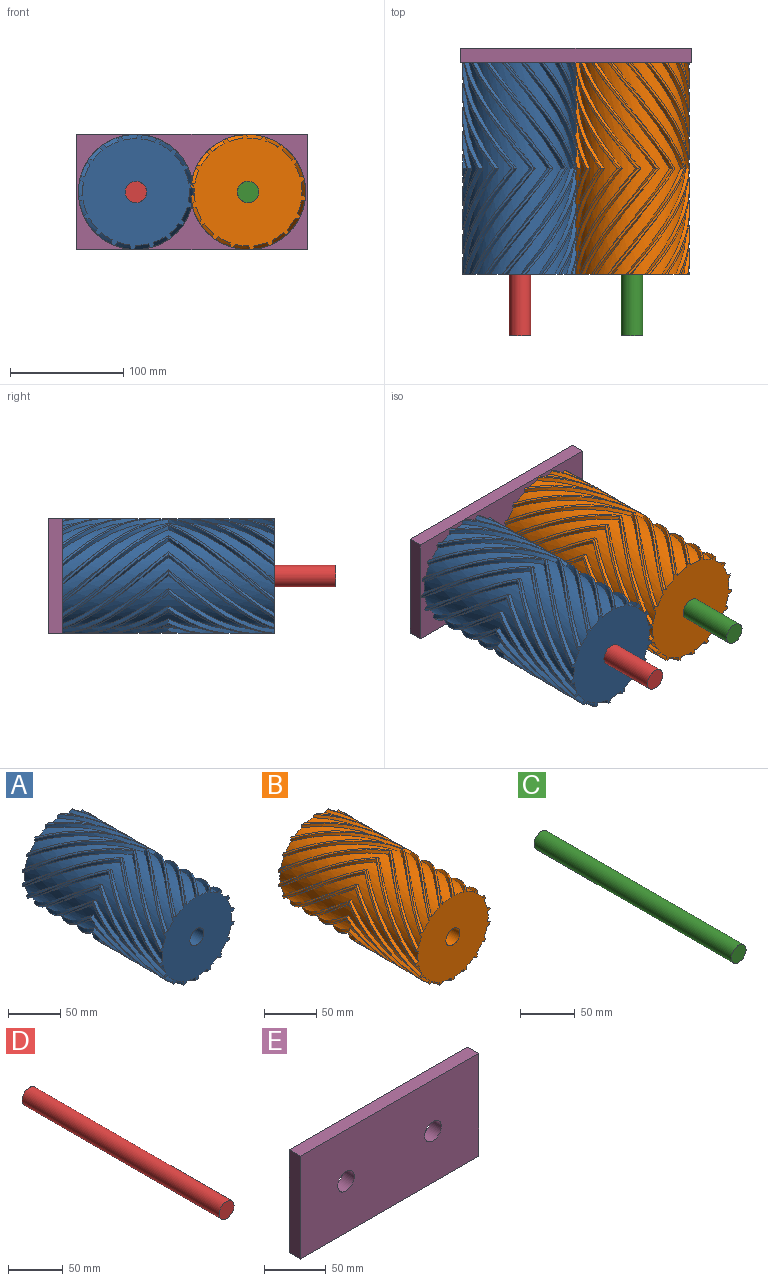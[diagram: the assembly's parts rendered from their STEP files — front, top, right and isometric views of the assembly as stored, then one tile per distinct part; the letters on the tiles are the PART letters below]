
ASSEMBLY  parts=5 mates=3
PART A: 129 faces, bbox 102.5x186.9x102.5 mm
  f0: plane 101.65x100.54mm, normal (0,-1,0), area 6946.6mm2, adj f1,f2,f3,f4,f5,f6,f7,f8
  f1: bspline ~93.47x69.89mm, area 471mm2, adj f0,f2,f4,f23
  f2: bspline ~93.47x71.15mm, area 235.9mm2, adj f0,f1,f3,f24
  f3: bspline ~93.47x68.96mm, area 471mm2, adj f0,f2,f16,f25
  f4: cylinder r=47.1mm len=186.94mm, axis (0,1,0), area 2157.7mm2, adj f0,f1,f22,f23,f97,f100
  f5: cylinder r=47.1mm len=186.94mm, axis (0,1,0), area 2157.7mm2, adj f0,f22,f31,f34,f35,f38
  f6: cylinder r=47.1mm len=186.94mm, axis (0,1,0), area 2157.7mm2, adj f0,f22,f37,f40,f41,f44
  f7: cylinder r=47.1mm len=186.94mm, axis (0,1,0), area 2157.7mm2, adj f0,f22,f43,f46,f47,f50
  f8: cylinder r=47.1mm len=186.94mm, axis (0,1,0), area 2157.7mm2, adj f0,f22,f49,f52,f53,f56
  f9: cylinder r=47.1mm len=186.94mm, axis (0,1,0), area 2157.7mm2, adj f0,f22,f55,f58,f59,f62
  f10: cylinder r=47.1mm len=186.94mm, axis (0,1,0), area 2157.7mm2, adj f0,f22,f61,f64,f65,f68
  f11: cylinder r=47.1mm len=186.94mm, axis (0,1,0), area 2157.7mm2, adj f0,f22,f67,f70,f77,f80
  f12: cylinder r=47.1mm len=186.94mm, axis (0,1,0), area 2157.7mm2, adj f0,f22,f73,f76,f89,f92
  f13: cylinder r=47.1mm len=186.94mm, axis (0,1,0), area 2157.7mm2, adj f0,f22,f71,f74,f79,f82
  f14: cylinder r=47.1mm len=186.94mm, axis (0,1,0), area 2157.7mm2, adj f0,f22,f85,f88,f95,f98
  f15: cylinder r=47.1mm len=186.94mm, axis (0,1,0), area 2157.7mm2, adj f0,f22,f83,f86,f91,f94
  f16: cylinder r=47.1mm len=186.94mm, axis (0,1,0), area 2157.7mm2, adj f0,f3,f22,f25,f26,f125
  f17: cylinder r=47.1mm len=186.94mm, axis (0,1,0), area 2157.7mm2, adj f0,f22,f103,f106,f113,f116
  f18: cylinder r=47.1mm len=186.94mm, axis (0,1,0), area 2157.7mm2, adj f0,f22,f29,f32,f109,f112
  f19: cylinder r=47.1mm len=186.94mm, axis (0,1,0), area 2157.7mm2, adj f0,f22,f115,f118,f119,f122
  f20: cylinder r=47.1mm len=186.94mm, axis (0,1,0), area 2157.7mm2, adj f0,f22,f107,f110,f121,f124
  f21: cylinder r=47.1mm len=186.94mm, axis (0,1,0), area 2157.7mm2, adj f0,f22,f28,f101,f104,f127
  f22: plane 101.65x100.54mm, normal (0,1,0), area 6946.6mm2, adj f4,f5,f6,f7,f8,f9,f10,f11
  f23: bspline ~93.47x69.89mm, area 471mm2, adj f1,f4,f22,f24
  f24: bspline ~93.47x71.15mm, area 235.9mm2, adj f2,f22,f23,f25
  f25: bspline ~93.47x68.96mm, area 471mm2, adj f3,f16,f22,f24
  f26: bspline ~93.47x60.41mm, area 471mm2, adj f16,f22,f27,f125
  f27: bspline ~93.47x60.34mm, area 235.9mm2, adj f22,f26,f28,f126
  f28: bspline ~93.47x57.85mm, area 471mm2, adj f21,f22,f27,f127
  f29: bspline ~93.47x53.27mm, area 471mm2, adj f18,f22,f30,f32
  f30: bspline ~93.47x52.25mm, area 235.9mm2, adj f22,f29,f31,f33
  f31: bspline ~93.47x53.27mm, area 471mm2, adj f5,f22,f30,f34
  f32: bspline ~93.47x53.27mm, area 471mm2, adj f0,f18,f29,f33
  f33: bspline ~93.47x52.25mm, area 235.9mm2, adj f0,f30,f32,f34
  f34: bspline ~93.47x53.27mm, area 471mm2, adj f0,f5,f31,f33
  f35: bspline ~93.47x64.39mm, area 471mm2, adj f0,f5,f36,f38
  f36: bspline ~93.47x66.76mm, area 235.9mm2, adj f0,f35,f37,f39
  f37: bspline ~93.47x66.03mm, area 471mm2, adj f0,f6,f36,f40
  f38: bspline ~93.47x64.39mm, area 471mm2, adj f5,f22,f35,f39
  f39: bspline ~93.47x66.76mm, area 235.9mm2, adj f22,f36,f38,f40
  f40: bspline ~93.47x66.03mm, area 471mm2, adj f6,f22,f37,f39
  f41: bspline ~93.47x71.45mm, area 471mm2, adj f0,f6,f42,f44
  f42: bspline ~93.47x73.38mm, area 235.9mm2, adj f0,f41,f43,f45
  f43: bspline ~93.47x71.76mm, area 471mm2, adj f0,f7,f42,f46
  f44: bspline ~93.47x71.45mm, area 471mm2, adj f6,f22,f41,f45
  f45: bspline ~93.47x73.38mm, area 235.9mm2, adj f22,f42,f44,f46
  f46: bspline ~93.47x71.76mm, area 471mm2, adj f7,f22,f43,f45
  f47: bspline ~93.47x69.89mm, area 471mm2, adj f0,f7,f48,f50
  f48: bspline ~93.47x71.15mm, area 235.9mm2, adj f0,f47,f49,f51
  f49: bspline ~93.47x68.96mm, area 471mm2, adj f0,f8,f48,f52
  f50: bspline ~93.47x69.89mm, area 471mm2, adj f7,f22,f47,f51
  f51: bspline ~93.47x71.15mm, area 235.9mm2, adj f22,f48,f50,f52
  f52: bspline ~93.47x68.96mm, area 471mm2, adj f8,f22,f49,f51
  f53: bspline ~93.47x60.41mm, area 471mm2, adj f0,f8,f54,f56
  f54: bspline ~93.47x60.34mm, area 235.9mm2, adj f0,f53,f55,f57
  f55: bspline ~93.47x57.85mm, area 471mm2, adj f0,f9,f54,f58
  f56: bspline ~93.47x60.41mm, area 471mm2, adj f8,f22,f53,f57
  f57: bspline ~93.47x60.34mm, area 235.9mm2, adj f22,f54,f56,f58
  f58: bspline ~93.47x57.85mm, area 471mm2, adj f9,f22,f55,f57
  f59: bspline ~93.47x57.85mm, area 471mm2, adj f0,f9,f60,f62
  f60: bspline ~93.47x60.34mm, area 235.9mm2, adj f0,f59,f61,f63
  f61: bspline ~93.47x60.41mm, area 471mm2, adj f0,f10,f60,f64
  f62: bspline ~93.47x57.85mm, area 471mm2, adj f9,f22,f59,f63
  f63: bspline ~93.47x60.34mm, area 235.9mm2, adj f22,f60,f62,f64
  f64: bspline ~93.47x60.41mm, area 471mm2, adj f10,f22,f61,f63
  f65: bspline ~93.47x68.96mm, area 471mm2, adj f0,f10,f66,f68
  f66: bspline ~93.47x71.15mm, area 235.9mm2, adj f0,f65,f67,f69
  f67: bspline ~93.47x69.89mm, area 471mm2, adj f0,f11,f66,f70
  f68: bspline ~93.47x68.96mm, area 471mm2, adj f10,f22,f65,f69
  f69: bspline ~93.47x71.15mm, area 235.9mm2, adj f22,f66,f68,f70
  f70: bspline ~93.47x69.89mm, area 471mm2, adj f11,f22,f67,f69
  f71: bspline ~93.47x66.03mm, area 471mm2, adj f0,f13,f72,f74
  f72: bspline ~93.47x66.76mm, area 235.9mm2, adj f0,f71,f73,f75
  f73: bspline ~93.47x64.39mm, area 471mm2, adj f0,f12,f72,f76
  f74: bspline ~93.47x66.03mm, area 471mm2, adj f13,f22,f71,f75
  f75: bspline ~93.47x66.76mm, area 235.9mm2, adj f22,f72,f74,f76
  f76: bspline ~93.47x64.39mm, area 471mm2, adj f12,f22,f73,f75
  f77: bspline ~93.47x71.76mm, area 471mm2, adj f0,f11,f78,f80
  f78: bspline ~93.47x73.38mm, area 235.9mm2, adj f0,f77,f79,f81
  f79: bspline ~93.47x71.45mm, area 471mm2, adj f0,f13,f78,f82
  f80: bspline ~93.47x71.76mm, area 471mm2, adj f11,f22,f77,f81
  f81: bspline ~93.47x73.38mm, area 235.9mm2, adj f22,f78,f80,f82
  f82: bspline ~93.47x71.45mm, area 471mm2, adj f13,f22,f79,f81
  f83: bspline ~93.47x64.39mm, area 471mm2, adj f0,f15,f84,f86
  f84: bspline ~93.47x66.76mm, area 235.9mm2, adj f0,f83,f85,f87
  f85: bspline ~93.47x66.03mm, area 471mm2, adj f0,f14,f84,f88
  f86: bspline ~93.47x64.39mm, area 471mm2, adj f15,f22,f83,f87
  f87: bspline ~93.47x66.76mm, area 235.9mm2, adj f22,f84,f86,f88
  f88: bspline ~93.47x66.03mm, area 471mm2, adj f14,f22,f85,f87
  f89: bspline ~93.47x53.27mm, area 471mm2, adj f0,f12,f90,f92
  f90: bspline ~93.47x52.25mm, area 235.9mm2, adj f0,f89,f91,f93
  f91: bspline ~93.47x53.27mm, area 471mm2, adj f0,f15,f90,f94
  f92: bspline ~93.47x53.27mm, area 471mm2, adj f12,f22,f89,f93
  f93: bspline ~93.47x52.25mm, area 235.9mm2, adj f22,f90,f92,f94
  f94: bspline ~93.47x53.27mm, area 471mm2, adj f15,f22,f91,f93
  f95: bspline ~93.47x71.45mm, area 471mm2, adj f0,f14,f96,f98
  f96: bspline ~93.47x73.38mm, area 235.9mm2, adj f0,f95,f97,f99
  f97: bspline ~93.47x71.76mm, area 471mm2, adj f0,f4,f96,f100
  f98: bspline ~93.47x71.45mm, area 471mm2, adj f14,f22,f95,f99
  f99: bspline ~93.47x73.38mm, area 235.9mm2, adj f22,f96,f98,f100
  f100: bspline ~93.47x71.76mm, area 471mm2, adj f4,f22,f97,f99
  f101: bspline ~93.47x57.85mm, area 471mm2, adj f21,f22,f102,f104
  f102: bspline ~93.47x60.34mm, area 235.9mm2, adj f22,f101,f103,f105
  f103: bspline ~93.47x60.41mm, area 471mm2, adj f17,f22,f102,f106
  f104: bspline ~93.47x57.85mm, area 471mm2, adj f0,f21,f101,f105
  f105: bspline ~93.47x60.34mm, area 235.9mm2, adj f0,f102,f104,f106
  f106: bspline ~93.47x60.41mm, area 471mm2, adj f0,f17,f103,f105
  f107: bspline ~93.47x66.03mm, area 471mm2, adj f20,f22,f108,f110
  f108: bspline ~93.47x66.76mm, area 235.9mm2, adj f22,f107,f109,f111
  f109: bspline ~93.47x64.39mm, area 471mm2, adj f18,f22,f108,f112
  f110: bspline ~93.47x66.03mm, area 471mm2, adj f0,f20,f107,f111
  f111: bspline ~93.47x66.76mm, area 235.9mm2, adj f0,f108,f110,f112
  f112: bspline ~93.47x64.39mm, area 471mm2, adj f0,f18,f109,f111
  f113: bspline ~93.47x68.96mm, area 471mm2, adj f17,f22,f114,f116
  f114: bspline ~93.47x71.15mm, area 235.9mm2, adj f22,f113,f115,f117
  f115: bspline ~93.47x69.89mm, area 471mm2, adj f19,f22,f114,f118
  f116: bspline ~93.47x68.96mm, area 471mm2, adj f0,f17,f113,f117
  f117: bspline ~93.47x71.15mm, area 235.9mm2, adj f0,f114,f116,f118
  f118: bspline ~93.47x69.89mm, area 471mm2, adj f0,f19,f115,f117
  f119: bspline ~93.47x71.76mm, area 471mm2, adj f19,f22,f120,f122
  f120: bspline ~93.47x73.38mm, area 235.9mm2, adj f22,f119,f121,f123
  f121: bspline ~93.47x71.45mm, area 471mm2, adj f20,f22,f120,f124
  f122: bspline ~93.47x71.76mm, area 471mm2, adj f0,f19,f119,f123
  f123: bspline ~93.47x73.38mm, area 235.9mm2, adj f0,f120,f122,f124
  f124: bspline ~93.47x71.45mm, area 471mm2, adj f0,f20,f121,f123
  f125: bspline ~93.47x60.41mm, area 471mm2, adj f0,f16,f26,f126
  f126: bspline ~93.47x60.34mm, area 235.9mm2, adj f0,f27,f125,f127
  f127: bspline ~93.47x57.85mm, area 471mm2, adj f0,f21,f28,f126
  f128: cylinder r=9.53mm len=186.94mm, axis (0,1,0), area 11188.1mm2, adj f0,f22
PART B: 129 faces, bbox 102.5x186.9x102.5 mm
  f0: plane 101.65x100.54mm, normal (0,-1,0), area 7058.5mm2, adj f1,f2,f3,f4,f5,f6,f7,f8
  f1: bspline ~93.47x69.89mm, area 406.7mm2, adj f0,f2,f4,f23
  f2: bspline ~93.47x71.15mm, area 235.9mm2, adj f0,f1,f3,f24
  f3: bspline ~93.47x68.96mm, area 406.7mm2, adj f0,f2,f16,f25
  f4: cylinder r=47.62mm len=186.94mm, axis (0,1,0), area 2227.2mm2, adj f0,f1,f22,f23,f97,f100
  f5: cylinder r=47.62mm len=186.94mm, axis (0,1,0), area 2227.2mm2, adj f0,f22,f31,f34,f35,f38
  f6: cylinder r=47.62mm len=186.94mm, axis (0,1,0), area 2227.2mm2, adj f0,f22,f37,f40,f41,f44
  f7: cylinder r=47.62mm len=186.94mm, axis (0,1,0), area 2227.2mm2, adj f0,f22,f43,f46,f47,f50
  f8: cylinder r=47.62mm len=186.94mm, axis (0,1,0), area 2227.2mm2, adj f0,f22,f49,f52,f53,f56
  f9: cylinder r=47.62mm len=186.94mm, axis (0,1,0), area 2227.2mm2, adj f0,f22,f55,f58,f59,f62
  f10: cylinder r=47.62mm len=186.94mm, axis (0,1,0), area 2227.2mm2, adj f0,f22,f61,f64,f65,f68
  f11: cylinder r=47.62mm len=186.94mm, axis (0,1,0), area 2227.2mm2, adj f0,f22,f67,f70,f77,f80
  f12: cylinder r=47.62mm len=186.94mm, axis (0,1,0), area 2227.2mm2, adj f0,f22,f73,f76,f89,f92
  f13: cylinder r=47.62mm len=186.94mm, axis (0,1,0), area 2227.2mm2, adj f0,f22,f71,f74,f79,f82
  f14: cylinder r=47.62mm len=186.94mm, axis (0,1,0), area 2227.2mm2, adj f0,f22,f85,f88,f95,f98
  f15: cylinder r=47.62mm len=186.94mm, axis (0,1,0), area 2227.2mm2, adj f0,f22,f83,f86,f91,f94
  f16: cylinder r=47.62mm len=186.94mm, axis (0,1,0), area 2227.2mm2, adj f0,f3,f22,f25,f26,f125
  f17: cylinder r=47.62mm len=186.94mm, axis (0,1,0), area 2227.2mm2, adj f0,f22,f103,f106,f113,f116
  f18: cylinder r=47.62mm len=186.94mm, axis (0,1,0), area 2227.2mm2, adj f0,f22,f29,f32,f109,f112
  f19: cylinder r=47.62mm len=186.94mm, axis (0,1,0), area 2227.2mm2, adj f0,f22,f115,f118,f119,f122
  f20: cylinder r=47.62mm len=186.94mm, axis (0,1,0), area 2227.2mm2, adj f0,f22,f107,f110,f121,f124
  f21: cylinder r=47.62mm len=186.94mm, axis (0,1,0), area 2227.2mm2, adj f0,f22,f28,f101,f104,f127
  f22: plane 101.65x100.54mm, normal (0,1,0), area 7058.5mm2, adj f4,f5,f6,f7,f8,f9,f10,f11
  f23: bspline ~93.47x69.89mm, area 406.7mm2, adj f1,f4,f22,f24
  f24: bspline ~93.47x71.15mm, area 235.9mm2, adj f2,f22,f23,f25
  f25: bspline ~93.47x68.96mm, area 406.7mm2, adj f3,f16,f22,f24
  f26: bspline ~93.47x60.41mm, area 406.7mm2, adj f16,f22,f27,f125
  f27: bspline ~93.47x60.34mm, area 235.9mm2, adj f22,f26,f28,f126
  f28: bspline ~93.47x57.85mm, area 406.7mm2, adj f21,f22,f27,f127
  f29: bspline ~93.47x53.18mm, area 406.7mm2, adj f18,f22,f30,f32
  f30: bspline ~93.47x52.25mm, area 235.9mm2, adj f22,f29,f31,f33
  f31: bspline ~93.47x53.18mm, area 406.7mm2, adj f5,f22,f30,f34
  f32: bspline ~93.47x53.18mm, area 406.7mm2, adj f0,f18,f29,f33
  f33: bspline ~93.47x52.25mm, area 235.9mm2, adj f0,f30,f32,f34
  f34: bspline ~93.47x53.18mm, area 406.7mm2, adj f0,f5,f31,f33
  f35: bspline ~93.47x64.39mm, area 406.7mm2, adj f0,f5,f36,f38
  f36: bspline ~93.47x66.76mm, area 235.9mm2, adj f0,f35,f37,f39
  f37: bspline ~93.47x66.02mm, area 406.7mm2, adj f0,f6,f36,f40
  f38: bspline ~93.47x64.39mm, area 406.7mm2, adj f5,f22,f35,f39
  f39: bspline ~93.47x66.76mm, area 235.9mm2, adj f22,f36,f38,f40
  f40: bspline ~93.47x66.02mm, area 406.7mm2, adj f6,f22,f37,f39
  f41: bspline ~93.47x71.45mm, area 406.7mm2, adj f0,f6,f42,f44
  f42: bspline ~93.47x73.38mm, area 235.9mm2, adj f0,f41,f43,f45
  f43: bspline ~93.47x71.76mm, area 406.7mm2, adj f0,f7,f42,f46
  f44: bspline ~93.47x71.45mm, area 406.7mm2, adj f6,f22,f41,f45
  f45: bspline ~93.47x73.38mm, area 235.9mm2, adj f22,f42,f44,f46
  f46: bspline ~93.47x71.76mm, area 406.7mm2, adj f7,f22,f43,f45
  f47: bspline ~93.47x69.89mm, area 406.7mm2, adj f0,f7,f48,f50
  f48: bspline ~93.47x71.15mm, area 235.9mm2, adj f0,f47,f49,f51
  f49: bspline ~93.47x68.96mm, area 406.7mm2, adj f0,f8,f48,f52
  f50: bspline ~93.47x69.89mm, area 406.7mm2, adj f7,f22,f47,f51
  f51: bspline ~93.47x71.15mm, area 235.9mm2, adj f22,f48,f50,f52
  f52: bspline ~93.47x68.96mm, area 406.7mm2, adj f8,f22,f49,f51
  f53: bspline ~93.47x60.41mm, area 406.7mm2, adj f0,f8,f54,f56
  f54: bspline ~93.47x60.34mm, area 235.9mm2, adj f0,f53,f55,f57
  f55: bspline ~93.47x57.85mm, area 406.7mm2, adj f0,f9,f54,f58
  f56: bspline ~93.47x60.41mm, area 406.7mm2, adj f8,f22,f53,f57
  f57: bspline ~93.47x60.34mm, area 235.9mm2, adj f22,f54,f56,f58
  f58: bspline ~93.47x57.85mm, area 406.7mm2, adj f9,f22,f55,f57
  f59: bspline ~93.47x57.85mm, area 406.7mm2, adj f0,f9,f60,f62
  f60: bspline ~93.47x60.34mm, area 235.9mm2, adj f0,f59,f61,f63
  f61: bspline ~93.47x60.41mm, area 406.7mm2, adj f0,f10,f60,f64
  f62: bspline ~93.47x57.85mm, area 406.7mm2, adj f9,f22,f59,f63
  f63: bspline ~93.47x60.34mm, area 235.9mm2, adj f22,f60,f62,f64
  f64: bspline ~93.47x60.41mm, area 406.7mm2, adj f10,f22,f61,f63
  f65: bspline ~93.47x68.96mm, area 406.7mm2, adj f0,f10,f66,f68
  f66: bspline ~93.47x71.15mm, area 235.9mm2, adj f0,f65,f67,f69
  f67: bspline ~93.47x69.89mm, area 406.7mm2, adj f0,f11,f66,f70
  f68: bspline ~93.47x68.96mm, area 406.7mm2, adj f10,f22,f65,f69
  f69: bspline ~93.47x71.15mm, area 235.9mm2, adj f22,f66,f68,f70
  f70: bspline ~93.47x69.89mm, area 406.7mm2, adj f11,f22,f67,f69
  f71: bspline ~93.47x66.02mm, area 406.7mm2, adj f0,f13,f72,f74
  f72: bspline ~93.47x66.76mm, area 235.9mm2, adj f0,f71,f73,f75
  f73: bspline ~93.47x64.39mm, area 406.7mm2, adj f0,f12,f72,f76
  f74: bspline ~93.47x66.02mm, area 406.7mm2, adj f13,f22,f71,f75
  f75: bspline ~93.47x66.76mm, area 235.9mm2, adj f22,f72,f74,f76
  f76: bspline ~93.47x64.39mm, area 406.7mm2, adj f12,f22,f73,f75
  f77: bspline ~93.47x71.76mm, area 406.7mm2, adj f0,f11,f78,f80
  f78: bspline ~93.47x73.38mm, area 235.9mm2, adj f0,f77,f79,f81
  f79: bspline ~93.47x71.45mm, area 406.7mm2, adj f0,f13,f78,f82
  f80: bspline ~93.47x71.76mm, area 406.7mm2, adj f11,f22,f77,f81
  f81: bspline ~93.47x73.38mm, area 235.9mm2, adj f22,f78,f80,f82
  f82: bspline ~93.47x71.45mm, area 406.7mm2, adj f13,f22,f79,f81
  f83: bspline ~93.47x64.39mm, area 406.7mm2, adj f0,f15,f84,f86
  f84: bspline ~93.47x66.76mm, area 235.9mm2, adj f0,f83,f85,f87
  f85: bspline ~93.47x66.02mm, area 406.7mm2, adj f0,f14,f84,f88
  f86: bspline ~93.47x64.39mm, area 406.7mm2, adj f15,f22,f83,f87
  f87: bspline ~93.47x66.76mm, area 235.9mm2, adj f22,f84,f86,f88
  f88: bspline ~93.47x66.02mm, area 406.7mm2, adj f14,f22,f85,f87
  f89: bspline ~93.47x53.18mm, area 406.7mm2, adj f0,f12,f90,f92
  f90: bspline ~93.47x52.25mm, area 235.9mm2, adj f0,f89,f91,f93
  f91: bspline ~93.47x53.18mm, area 406.7mm2, adj f0,f15,f90,f94
  f92: bspline ~93.47x53.18mm, area 406.7mm2, adj f12,f22,f89,f93
  f93: bspline ~93.47x52.25mm, area 235.9mm2, adj f22,f90,f92,f94
  f94: bspline ~93.47x53.18mm, area 406.7mm2, adj f15,f22,f91,f93
  f95: bspline ~93.47x71.45mm, area 406.7mm2, adj f0,f14,f96,f98
  f96: bspline ~93.47x73.38mm, area 235.9mm2, adj f0,f95,f97,f99
  f97: bspline ~93.47x71.76mm, area 406.7mm2, adj f0,f4,f96,f100
  f98: bspline ~93.47x71.45mm, area 406.7mm2, adj f14,f22,f95,f99
  f99: bspline ~93.47x73.38mm, area 235.9mm2, adj f22,f96,f98,f100
  f100: bspline ~93.47x71.76mm, area 406.7mm2, adj f4,f22,f97,f99
  f101: bspline ~93.47x57.85mm, area 406.7mm2, adj f21,f22,f102,f104
  f102: bspline ~93.47x60.34mm, area 235.9mm2, adj f22,f101,f103,f105
  f103: bspline ~93.47x60.41mm, area 406.7mm2, adj f17,f22,f102,f106
  f104: bspline ~93.47x57.85mm, area 406.7mm2, adj f0,f21,f101,f105
  f105: bspline ~93.47x60.34mm, area 235.9mm2, adj f0,f102,f104,f106
  f106: bspline ~93.47x60.41mm, area 406.7mm2, adj f0,f17,f103,f105
  f107: bspline ~93.47x66.02mm, area 406.7mm2, adj f20,f22,f108,f110
  f108: bspline ~93.47x66.76mm, area 235.9mm2, adj f22,f107,f109,f111
  f109: bspline ~93.47x64.39mm, area 406.7mm2, adj f18,f22,f108,f112
  f110: bspline ~93.47x66.02mm, area 406.7mm2, adj f0,f20,f107,f111
  f111: bspline ~93.47x66.76mm, area 235.9mm2, adj f0,f108,f110,f112
  f112: bspline ~93.47x64.39mm, area 406.7mm2, adj f0,f18,f109,f111
  f113: bspline ~93.47x68.96mm, area 406.7mm2, adj f17,f22,f114,f116
  f114: bspline ~93.47x71.15mm, area 235.9mm2, adj f22,f113,f115,f117
  f115: bspline ~93.47x69.89mm, area 406.7mm2, adj f19,f22,f114,f118
  f116: bspline ~93.47x68.96mm, area 406.7mm2, adj f0,f17,f113,f117
  f117: bspline ~93.47x71.15mm, area 235.9mm2, adj f0,f114,f116,f118
  f118: bspline ~93.47x69.89mm, area 406.7mm2, adj f0,f19,f115,f117
  f119: bspline ~93.47x71.76mm, area 406.7mm2, adj f19,f22,f120,f122
  f120: bspline ~93.47x73.38mm, area 235.9mm2, adj f22,f119,f121,f123
  f121: bspline ~93.47x71.45mm, area 406.7mm2, adj f20,f22,f120,f124
  f122: bspline ~93.47x71.76mm, area 406.7mm2, adj f0,f19,f119,f123
  f123: bspline ~93.47x73.38mm, area 235.9mm2, adj f0,f120,f122,f124
  f124: bspline ~93.47x71.45mm, area 406.7mm2, adj f0,f20,f121,f123
  f125: bspline ~93.47x60.41mm, area 406.7mm2, adj f0,f16,f26,f126
  f126: bspline ~93.47x60.34mm, area 235.9mm2, adj f0,f27,f125,f127
  f127: bspline ~93.47x57.85mm, area 406.7mm2, adj f0,f21,f28,f126
  f128: cylinder r=9.53mm len=186.94mm, axis (0,1,0), area 11188.1mm2, adj f0,f22
PART C: 3 faces, bbox 19.1x254x19.1 mm
  f0: cylinder r=9.53mm len=254mm, axis (0,1,0), area 15201.2mm2, adj f1,f2
  f1: plane 19.05x19.05mm, normal (0,-1,0), area 285mm2, adj f0
  f2: plane 19.05x19.05mm, normal (0,1,0), area 285mm2, adj f0
PART D: 3 faces, bbox 19.1x254x19.1 mm
  f0: cylinder r=9.53mm len=254mm, axis (0,1,0), area 15201.2mm2, adj f1,f2
  f1: plane 19.05x19.05mm, normal (0,-1,0), area 285mm2, adj f0
  f2: plane 19.05x19.05mm, normal (0,1,0), area 285mm2, adj f0
PART E: 8 faces, bbox 203.2x12.7x101.6 mm
  f0: plane 101.6x12.7mm, normal (-1,0,0), area 1290.3mm2, adj f1,f4,f6,f7
  f1: plane 203.2x12.7mm, normal (0,0,-1), area 2580.6mm2, adj f0,f2,f6,f7
  f2: plane 101.6x12.7mm, normal (1,0,0), area 1290.3mm2, adj f1,f4,f6,f7
  f3: cylinder r=9.53mm len=19.05mm, axis (0,-1,0), area 760.1mm2, adj f6,f7
  f4: plane 203.2x12.7mm, normal (0,0,1), area 2580.6mm2, adj f0,f2,f6,f7
  f5: cylinder r=9.53mm len=19.05mm, axis (0,-1,0), area 760.1mm2, adj f6,f7
  f6: plane 203.2x101.6mm, normal (0,1,0), area 20075.1mm2, adj f0,f1,f2,f3,f4,f5
  f7: plane 203.2x101.6mm, normal (0,-1,0), area 20075.1mm2, adj f0,f1,f2,f3,f4,f5
PLACE A rot(axis=(0,1,0),163.5deg) t=(136.91,27.84,20.51)mm
PLACE B rot(axis=(0,-1,0),163.5deg) t=(235.97,27.84,20.51)mm
PLACE C t=(186.44,134.02,20.51)mm
PLACE D t=(186.44,134.02,20.51)mm
PLACE E t=(186.44,121.32,20.51)mm fixed
MATE revolute A.f4 <-> E.f3  axis (0,1,0) through (136.91,121.32,20.51)mm
MATE fastened C.f0 <-> E.f5  axis (0,1,0) through (235.97,134.02,20.51)mm
MATE revolute B.f4 <-> E.f5  axis (0,1,0) through (235.97,121.32,20.51)mm
